# Revit family: Maxlogic извещатели линейного типа
name_source: partatom
category: Fire Alarm Devices
units: mm (PartAtom-declared; Revit-internal decimal feet)

## family parameters
Cut with Voids When Loaded = No
Host = Face
Maintain Annotation Orientation = Yes
OmniClass Number = 23.85.30.21
OmniClass Title = Environmental Detection/Registration
Part Type = Normal
Room Calculation Point = No
Round Connector Dimension = Use Diameter
Shared = No

## types (6) — shared parameters
Manufacturer = Mavili Elektronik Ticaret A.Ş.
Model = MaxLogic
URL = https://www.mavili.com.tr
Адрес №1 = Şerifali Mahallesi Kutup Sokak No:27/1-2-4 Ümraniye TR-34775 İSTANBUL
Вес = 830 гр
Вторичный материал = Пластмассовый
Гарантийный срок запчастей = 2
Гарантия срока службы = 2
Главный Материал = Белый пластмассовый PC/ABS
Инструкция по установке = https://mavilielektronik.com
Монтажная высота = Ниже потолка на 10% от высоты.
Монтажная поверхность = Настенная
Номер телефона = (+)90 216 466 45 05
Номер факса = (+)90 216 466 45 10
Номинальная высота = 160 мм
Номинальная глубина = 109 мм
Номинальная ширина = 192 мм
Рабочая Температура = (-10°C) - (+55°C)
Резервное питание = 24 В Пост. ток
Цвет = Белый
zero-valued in all types: Cost, Default Elevation

## per-type parameters (varying)
| type | Description | Гарантийный срок | Код продукта | Настройка адреса устройства | Номер позы общественных работ | Производительность кода | Рабочее напряжение (по умолчанию) | рефлектор |
| Maxlogic Дымовой линейный извещатель адресный (вкл. излучатель и приемник) | Дымовой линейный извещатель адресный (вкл. излучатель и приемник) | Year | ML-1170 | Модульная адресация |  | EN 54-12 и EN 54-17 | 20V - 30 В Пост. ток |  |
| Maxlogic Дымовой линейный извещатель адресный (вкл. излучатель и приемник) с изолятором КЗ | Дымовой линейный извещатель адресный (вкл. излучатель и приемник) с изолятором КЗ | Года | ML-1170.SCI | Модульная адресация |  | EN 54-12 ve EN 54-17 | 20V - 30В Пост. ток |  |
| Maxlogic Адресный линейный извещатель, однокомпонентный , вкл. отражатель | Адресный линейный извещатель, однокомпонентный , вкл. отражатель | Года | ML-1173 | Модульная адресация |  | EN 54-12 и EN 54-17 | 20V - 30В Пост. ток | ML-0171 ve ML-0174 |
| Maxlogic Адресный линейный извещатель, однокомпонентный , вкл. отражатель с изолятором КЗ | Адресный линейный извещатель, однокомпонентный , вкл. отражатель с изолятором КЗ | Года | ML-1173.SCI | Модульная адресация |  | EN 54-12 и EN 54-17 | 20V - 30В Пост. ток | ML-0171 ve ML-0174 |
| Maxlogic Дымовой линейный извещатель неадресный (вкл. излучатель и приемник) | Дымовой линейный извещатель неадресный (вкл. излучатель и приемник) | Года | ML-2170 |  | 832-111 | EN 54-12 и EN 54-17 | 20V - 30В Пост. ток |  |
| Maxlogic Недресный линейный извещатель, однокомпонентный , вкл. отражатель | Недресный линейный извещатель, однокомпонентный , вкл. отражатель | Года | ML-2173 |  |  | EN 54-12 и EN 54-17 | 20V - 30В Пост. ток | ML-0171 ve ML-0174 |

## geometry (parser evidence)
native form markers: Sweep x2
no freeform markers — native parametric forms only
